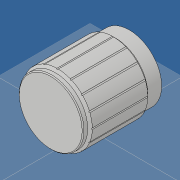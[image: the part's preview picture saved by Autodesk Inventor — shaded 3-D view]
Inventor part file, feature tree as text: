
AUTODESK INVENTOR PART (.ipt)
format: ipt  version: 2019 (Build 230136000, 136)  size: 199,168 bytes
history: native  units: mm
features: extrude x3, chamfer x2, sketch x1
ambient origin geometry x8: Origin, YZ Plane, XZ Plane, XY Plane, X Axis, Y Axis, Z Axis, Center Point
bodies: Volumenkörper1 (feature_tree)
feature tree (6):
  sketch  "Skizze1"  dims[d0=15.0mm d1=17.0mm d2=0.0mm d3=14.0mm d4=7.0mm d5=5.0mm d6=0.0mm d7=0.0mm d8=0.5mm d9=2.0mm d10=45.0deg d11=0.2mm d12=2.0mm d13=45.0deg d14=6.0mm d15=1.5mm d16=8.5mm d17=0.0mm d18=0.0mm d20=0.3mm d21=0.1mm d22=160.0mm d24=360.0deg]
  extrude  "Extrusion1"  Depth=17.0mm TaperAngle=0.0deg
  extrude  "Extrusion2"  Depth=8.5mm
  chamfer  "Fase1"  Distance=7.0mm
  chamfer  "Fase2"  Distance=0.5mm Angle=45.0deg
  extrude  "Extrusion3"  Depth=8.5mm TaperAngle=45.0deg
